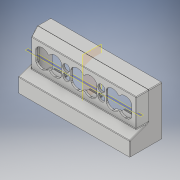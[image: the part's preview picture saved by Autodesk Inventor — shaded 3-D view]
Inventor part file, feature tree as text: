
AUTODESK INVENTOR PART (.ipt)
format: ipt  version: 2019 (Build 230136000, 136)  size: 1,297,920 bytes
history: native  units: mm
features: reference x101, sketch x54, extrude x48, projected_geometry x15, other x14, plane x14, mirror x9, hole x5, fillet x4, pattern_linear x2
ambient origin geometry x8: Origin, YZ Plane, XZ Plane, XY Plane, X Axis, Y Axis, Z Axis, Center Point
bodies: Body1 (feature_tree)
feature tree (266):
  other  "Querschnitt1"
  extrude  "Extrusion2"  Depth=3.0mm TaperAngle=0.0deg
  extrude  "Extrusion3"  TaperAngle=0.0deg  [1 undecoded]
  extrude  "Extrusion4"  Depth=4.0mm TaperAngle=0.0deg
  extrude  "Extrusion5"  Depth=1.5mm
  extrude  "Extrusion6"  Depth=0.5mm
  extrude  "Extrusion7"  Depth=0.5mm
  extrude  "Extrusion8"  Depth=13.0mm
  fillet  "Rundung1"  Radius=45.0mm
  extrude  "Extrusion9"  Depth=12.217305mm
  hole  "Bohrung1"  [1 undecoded]
  plane  "Arbeitsebene9"
  plane  "Arbeitsebene10"
  plane  "Arbeitsebene11"
  plane  "Arbeitsebene12"
  plane  "Arbeitsebene13"
  extrude  "Extrusion17"  Depth=3.0mm
  plane  "Arbeitsebene14"
  plane  "Arbeitsebene15"
  mirror  "Spiegeln4"
  extrude  "Extrusion18"  Depth=30.0mm TaperAngle=0.0deg
  extrude  "Extrusion19"  Depth=30.0mm TaperAngle=0.0deg
  extrude  "Extrusion20"  Depth=100.0mm
  mirror  "Spiegeln5"
  mirror  "Spiegeln6"
  mirror  "Spiegeln7"
  plane  "Arbeitsebene21"
  extrude  "Extrusion21"  TaperAngle=0.0deg  [1 undecoded]
  extrude  "Extrusion43"  Depth=4.0mm
  extrude  "Extrusion44"  Depth=20.0mm TaperAngle=0.0deg
  extrude  "Extrusion45"  Depth=15.0mm
  plane  "Arbeitsebene22"
  extrude  "Extrusion46"  Depth=100.0mm TaperAngle=0.0deg
  extrude  "Extrusion47"  Depth=12.0mm TaperAngle=0.0deg
  extrude  "Extrusion48"  Depth=2.0mm
  extrude  "Extrusion49"  Depth=1.0mm
  extrude  "Extrusion50"  Depth=2.0mm
  extrude  "Extrusion51"  Depth=1.5mm
  extrude  "Extrusion52"  Depth=5.0mm
  extrude  "Extrusion53"  Depth=10.0mm TaperAngle=0.0deg
  extrude  "Extrusion54"  Depth=10.0mm
  hole  "Bohrung4"  [1 undecoded]
  extrude  "Extrusion55"  Depth=10.0mm
  mirror  "Spiegeln10"
  extrude  "Extrusion56"  Depth=2.5mm
  extrude  "Extrusion57"  Depth=2.0mm
  extrude  "Extrusion58"  Depth=7.0mm
  extrude  "Extrusion59"  Depth=6.0mm
  fillet  "Rundung3"  Radius=4.0mm
  pattern_linear  "Rechteckige Anordnung2"  Spacing1=3.0mm  [1 undecoded]
  fillet  "Rundung4"  Radius=3.490659mm
  extrude  "Extrusion60"  Depth=3.0mm
  mirror  "Spiegeln11"
  hole  "Bohrung5"  [1 undecoded]
  sketch  "Skizze77"  dims[d196=8.5mm d197=0.0mm]
  extrude  "Extrusion61"  Depth=20.0mm TaperAngle=0.0deg
  mirror  "Spiegeln12"
  extrude  "Extrusion22"  Depth=20.0mm TaperAngle=0.0deg
  sketch  "Skizze31"  dims[d81=100.0mm d82=0.0mm d83=0.0mm]
  extrude  "Extrusion23"  TaperAngle=0.0deg  [1 undecoded]
  extrude  "Extrusion24"  Depth=20.0mm TaperAngle=0.0deg
  plane  "Arbeitsebene16"
  plane  "Arbeitsebene17"
  sketch  "Skizze34"  dims[d84=39.0mm d85=0.0mm d87=4.0mm]
  plane  "Arbeitsebene19"
  extrude  "Extrusion27"  Depth=3.0mm
  extrude  "Extrusion28"  Depth=5.5mm
  extrude  "Extrusion29"  Depth=5.5mm TaperAngle=0.0deg
  hole  "Bohrung2"  [1 undecoded]
  pattern_linear  "Rechteckige Anordnung1"  Count1=2 Spacing1=0.0mm
  extrude  "Extrusion30"  Depth=3.0mm TaperAngle=0.0deg
  plane  "Arbeitsebene20"
  extrude  "Extrusion34"  Depth=10.0mm
  extrude  "Extrusion35"  Depth=10.0mm
  extrude  "Extrusion36"  Depth=10.0mm
  extrude  "Extrusion37"  Depth=10.0mm
  extrude  "Extrusion38"  Depth=5.5mm TaperAngle=0.0deg
  extrude  "Extrusion39"  Depth=7.5mm
  extrude  "Extrusion40"  Depth=5.5mm
  extrude  "Extrusion41"  Depth=5.5mm
  mirror  "Spiegeln8"
  hole  "Bohrung3"  [1 undecoded]
  extrude  "Extrusion42"  Depth=2.0mm
  mirror  "Spiegeln9"
  fillet  "Rundung2"  Radius=99.5mm
  sketch  "Skizze1"  dims[d3=3.0mm d4=0.0mm d5=4.0mm d6=0.0mm]
  reference  "Referenz1"
  reference  "Referenz2"
  reference  "Referenz3"
  reference  "Referenz4"
  reference  "Referenz5"
  reference  "Referenz6"
  reference  "Referenz7"
  reference  "Referenz8"
  sketch  "Skizze2"  dims[d7=4.0mm d8=0.0mm d9=0.0mm d10=0.0mm]
  reference  "Referenz9"
  reference  "Referenz10"
  reference  "Referenz11"
  reference  "Referenz12"
  reference  "Referenz13"
  reference  "Referenz14"
  reference  "Referenz15"
  reference  "Referenz16"
  reference  "Referenz17"
  reference  "Referenz18"
  reference  "Referenz19"
  reference  "Referenz20"
  sketch  "Skizze3"  dims[d11=4.0mm d12=0.0mm d13=4.0mm d14=0.0mm]
  reference  "Referenz21"
  reference  "Referenz22"
  reference  "Referenz23"
  reference  "Referenz24"
  reference  "Referenz25"
  reference  "Referenz26"
  reference  "Referenz27"
  reference  "Referenz28"
  reference  "Referenz29"
  reference  "Referenz30"
  reference  "Referenz31"
  reference  "Referenz32"
  sketch  "Skizze4"  dims[d15=4.0mm d16=0.0mm d17=1.5mm]
  reference  "Referenz33"
  reference  "Referenz34"
  reference  "Referenz35"
  reference  "Referenz36"
  reference  "Referenz37"
  reference  "Referenz38"
  reference  "Referenz39"
  reference  "Referenz40"
  reference  "Referenz41"
  reference  "Referenz42"
  reference  "Referenz43"
  reference  "Referenz44"
  reference  "Referenz45"
  reference  "Referenz46"
  reference  "Referenz47"
  reference  "Referenz48"
  reference  "Referenz49"
  reference  "Referenz50"
  reference  "Referenz51"
  reference  "Referenz52"
  reference  "Referenz53"
  reference  "Referenz54"
  reference  "Referenz55"
  reference  "Referenz56"
  sketch  "Skizze5"  dims[d18=170.0mm d19=0.5mm]
  reference  "Referenz57"
  reference  "Referenz58"
  reference  "Referenz59"
  reference  "Referenz60"
  reference  "Referenz61"
  reference  "Referenz62"
  reference  "Referenz63"
  reference  "Referenz64"
  reference  "Referenz65"
  reference  "Referenz66"
  reference  "Referenz67"
  reference  "Referenz68"
  sketch  "Skizze6"  dims[d20=0.5mm d21=0.5mm]
  reference  "Referenz69"
  reference  "Referenz70"
  reference  "Referenz71"
  reference  "Referenz72"
  reference  "Referenz73"
  reference  "Referenz74"
  reference  "Referenz75"
  reference  "Referenz76"
  reference  "Referenz77"
  reference  "Referenz78"
  reference  "Referenz79"
  reference  "Referenz80"
  sketch  "Skizze7"  dims[d22=4.0mm d23=0.0mm d24=13.0mm]
  reference  "Referenz81"
  reference  "Referenz82"
  reference  "Referenz83"
  reference  "Referenz84"
  reference  "Referenz85"
  reference  "Referenz86"
  reference  "Referenz87"
  reference  "Referenz88"
  reference  "Referenz89"
  reference  "Referenz90"
  reference  "Referenz91"
  reference  "Referenz92"
  sketch  "Skizze8"  dims[d25=11.5mm d26=6.0mm d27=7.5mm d28=2.0mm d29=90.0deg d30=10.65mm d31=20.594885mm]
  projected_geometry  "Projizierte Kontur1"
  sketch  "Skizze9"  dims[d42=0.5mm d43=2.0mm d44=0.0mm d45=20.0mm d61=45.0mm]
  sketch  "Skizze24"  dims[d63=12.217305mm d64=12.217305mm]
  sketch  "Skizze26"  dims[d65=12.217305mm d66=90.0deg]
  sketch  "Skizze27"  dims[d69=90.0deg d70=3.0mm]
  projected_geometry  "Projizierte Kontur3"
  sketch  "Skizze28"  dims[d71=30.0mm d72=0.0mm d73=30.0mm d74=0.0mm]
  projected_geometry  "Projizierte Kontur4"
  sketch  "Skizze29"  dims[d75=30.0mm d76=0.0mm d77=30.0mm d78=0.0mm]
  sketch  "Skizze30"  dims[d79=15.0mm d80=100.0mm]
  projected_geometry  "Projizierte Kontur5"
  projected_geometry  "Projizierte Kontur6"
  projected_geometry  "Projizierte Kontur7"
  sketch  "Skizze36"  dims[d88=20.0mm d89=0.0mm d90=20.0mm d91=0.0mm]
  sketch  "Skizze37"  dims[d92=12.217305mm d98=15.0mm]
  sketch  "Skizze38"  dims[d99=100.0mm d100=0.0mm d101=100.0mm d102=0.0mm]
  reference  "Referenz98"
  sketch  "Skizze39"  dims[d103=1.0mm d104=12.0mm d105=12.0mm d106=0.0mm d107=0.0mm]
  sketch  "Skizze41"  dims[d108=2.0mm d109=0.14mm]
  projected_geometry  "Projizierte Kontur11"
  sketch  "Skizze45"  dims[d110=1.65mm d111=1.0mm]
  sketch  "Skizze46"  dims[d112=1.0mm d113=2.0mm]
  sketch  "Skizze47"  dims[d114=16.0mm d115=1.5mm]
  sketch  "Skizze48"  dims[d116=1.5mm d117=6.0mm d118=4.0mm d119=2.0mm d120=90.0deg d121=5.0mm d122=20.594885mm d123=30.0mm d125=57.0mm]
  sketch  "Skizze49"  dims[d126=10.0mm d128=10.0mm d129=4.0mm d130=0.0mm]
  sketch  "Skizze50"  dims[d134=-1.0mm d146=10.0mm]
  sketch  "Skizze51"  dims[d147=10.0mm d148=46.0mm d149=0.0mm]
  projected_geometry  "Projizierte Kontur13"
  sketch  "Skizze52"  dims[d150=10.0mm d151=10.0mm]
  sketch  "Skizze53"  dims[d152=46.0mm d153=0.0mm d154=2.5mm]
  projected_geometry  "Projizierte Kontur14"
  sketch  "Skizze54"  dims[d155=2.0mm d156=1.0mm]
  projected_geometry  "Projizierte Kontur15"
  sketch  "Skizze56"  dims[d157=47.0mm d158=0.0mm d162=7.0mm]
  sketch  "Skizze57"  dims[d163=2.5mm d164=6.0mm d165=4.0mm]
  sketch  "Skizze59"  dims[d166=98.0mm]
  sketch  "Skizze60"  dims[d167=46.0mm d168=0.0mm]
  sketch  "Skizze61"  dims[d169=2.0mm]
  sketch  "Skizze62"  dims[d171=99.2mm]
  projected_geometry  "Projizierte Kontur16"
  sketch  "Skizze63"  dims[d172=47.0mm d173=0.0mm]
  sketch  "Skizze64"  dims[d174=51.7mm]
  sketch  "Skizze65"  dims[d175=2.0mm]
  sketch  "Skizze66"  dims[d176=1.0mm]
  sketch  "Skizze67"  dims[d177=47.0mm d178=0.0mm]
  sketch  "Skizze68"  dims[d179=47.0mm d180=0.0mm]
  sketch  "Skizze69"  dims[d181=0.872665mm]
  projected_geometry  "Projizierte Kontur17"
  projected_geometry  "Projizierte Kontur18"
  sketch  "Skizze70"  dims[d182=3.0mm]
  plane  "Arbeitsebene23"
  sketch  "Skizze71"  dims[d183=4.0mm]
  reference  "Referenz99"
  reference  "Referenz100"
  projected_geometry  "Projizierte Kontur19"
  reference  "Referenz101"
  sketch  "Skizze72"  dims[d184=47.0mm d185=0.0mm]
  reference  "Referenz102"
  sketch  "Skizze73"  dims[d186=3.5mm d187=6.0mm d188=4.0mm d189=2.0mm d190=90.0deg d191=15.0mm d192=20.594885mm]
  reference  "Referenz103"
  sketch  "Skizze74"  dims[d193=5.8mm]
  reference  "Referenz104"
  reference  "Referenz105"
  reference  "Referenz106"
  sketch  "Skizze75"  dims[d194=2.8mm]
  projected_geometry  "Projizierte Kontur20"
  sketch  "Skizze76"  dims[d195=5.0mm]
  sketch  "Skizze78"  dims[d198=4.0mm d199=3.0mm d200=3.490659mm d201=3.0mm d202=17.0mm d203=0.0mm d204=20.0mm d205=0.0mm d206=20.0mm d207=0.0mm d208=0.0mm d209=0.0mm d211=20.0mm d212=0.0mm d213=3.0mm d214=49.0mm d215=1.0mm d216=0.0mm d217=20.0mm d218=0.0mm d219=20.0mm d220=0.0mm d221=3.0mm d222=0.0mm d223=10.0mm d224=10.0mm d225=10.0mm d226=10.0mm d227=46.0mm d228=0.0mm d229=7.5mm d230=6.0mm d231=97.0mm d232=45.0mm d233=0.0mm d234=2.0mm d235=99.5mm d236=1.2mm d237=1.5mm d238=47.0mm d239=0.0mm d241=53.0mm d242=1.5mm d243=47.0mm d244=0.0mm d245=2.9mm d246=6.0mm d247=4.0mm d248=2.0mm d249=90.0deg d250=15.0mm d251=20.594885mm d252=2.2mm d253=5.0mm d254=3.0mm d255=8.5mm d256=0.0mm d257=1.0mm d258=0.2mm d259=1.0mm d260=0.2mm d261=0.2mm d262=20.0mm d263=0.0mm d264=0.1mm d265=10.0mm d266=10.0mm d267=1.0mm d268=20.0mm d269=0.0mm d270=0.1mm d271=16.0mm d272=0.0mm d273=1.0mm d274=0.1mm d275=1.1mm d276=0.1mm d277=16.0mm d278=0.0mm d279=2.0mm d280=30.0mm d282=57.0mm d283=1.0mm d284=12.825mm d285=0.0mm d286=2.0mm d287=114.0mm d288=2.9mm d289=6.0mm d290=5.5mm d291=2.0mm d292=90.0deg d293=10.0mm d294=20.594885mm d295=2.2mm d296=5.0mm d297=3.0mm d298=5.5mm d299=0.0mm]
  parser-record x2  (decoder bookkeeping rows leaked as tree rows — omitted from the tree; the rows remain in map.json)
  other  "Zusammenbau.iam"
  other  "IN-12a:1"
  other  "IN-12a:2"
  other  "IN-12a:3"
  other  "IN-12a:4"
  other  "IN-12a:5"
  other  "IN-12a:6"
  other  "NixieModule_IN12.brd:2"
  other  "IN-12_Nixie_Board_Zusammenbau.iam"
  other  "IN-12_Nixie_Board:1"
  other  "NixieModule_IN12.brd:1"
note: 9 required parameter values undecoded (feature->parameter linkage not recoverable at this tier; creation-order binding heuristic only, values carry confidence <= 0.55)
note: 2 file-system paths scrubbed to <path> (originals preserved in map.json)
